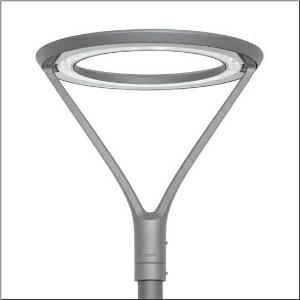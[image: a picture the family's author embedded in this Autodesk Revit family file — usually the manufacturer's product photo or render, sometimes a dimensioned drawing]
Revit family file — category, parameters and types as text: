
# Revit family: dl_r__20___pl1_2s_5xa51283ns008_3424
name_source: partatom
category: Lighting Fixtures
units: mm (PartAtom-declared; Revit-internal decimal feet)

## family parameters
Cut with Voids When Loaded = No
Host = Face
Light Source = No
Part Type = Normal
Room Calculation Point = No
Round Connector Dimension = Use Diameter
Shared = No

## types (1)
- --- (1 x LED, 3060 lm, 23.2 W, 4000K)
    Apparent Load = 23 VA
    CIE Flux Codes = 33 78 99 100 100
    Color Rendering = 70
    Color Temperature = 4000K
    Default Elevation = 1800 mm
    Description = DL® 20, mast luminaire, primary light control with reflector, highly specular, primary optical cover: cover, of toughened safety glass of clear glass with excellent transmission level, light distribution: PL1.2s, light emission: direct distribution, primary light characteristic: symmetric, installation type: post-top, LED, High Power LED, rated luminous flux: 3.030lm, luminous efficacy: 111lm/W, light colour: 740, colour temperature: 4000K, control gear: Plus, control: overheat protection, power reduction, digital communication interface, constant luminous flux control, time-dependent luminous flux control, flexible luminous flux parameterisation, electronic power reduction, mains connection: 230..240V, 50/60Hz, connection cable pre-assembled, cable length: 5m, start of lifetime: 27W, end of service life: 28W, reduction: 14W, luminaire housing, upper part, of cast aluminium, powder-coated, Siteco® metallic grey (DB 702S), diameter: 690mm, height: 690mm, spigot size: 76mm (post-top), mounting height: 4..6m, luminaire housing, of cast aluminium, powder-coated, Siteco® metallic grey (DB 702S), equipment: standard, protection rating (complete): IP66, insulation class (complete): insulation class II (safety insulation), certification: CE, ENEC, VDE, impact resistance: IK08, permissible operating ambient temperature: -25..+35°C, standard-compliant lighting for roads and squares, packaging unit: 1 piece

Light Distribution: PL1.2s
    Height = 690 mm
    Lamp = 1 x LED
    Lamp Light Flux = 3060 lm
    Lamp Power = 23.2 W
    Lamp count = 1
    Length = 690 mm
    Luminous efficacy = 132 lm/W
    Manufacturer = Siteco
    ModVariant = No
    Model = 5XA51283NS008
    Number of Poles = 1
    OnlyDefault = Yes
    Power Factor = 1
    Product Name = DL® 20 | PL1.2s
    Product group = mast luminaire | pylon top
    ProductGroupID = 6100
    Protection Class = Protection class II
    Protection Degree = IP 66
    RLX_Detail_Level = 1
    RLX_Emergency_Light_Flux = 0 lm
    RLX_Emergency_Type = 0
    RLX_Emergency_Type_DB = No
    RlxData = <blob elided: 204313 chars, md5=7895c937>
    Socket = socket
    Standby Power = 0 W
    System Light Flux = 3060 lm
    System Power = 23 W
    Type Comments = factory setting: luminous flux: 100 % | dim-lin: 254 | 310 mA
    Type Image = l_1006001.jpg
    URL = http://relux.com
    VarID = @adj_098159
    Voltage = 0 V
    Weight = 0.00 kg
    Width = 0 mm  [stored 0 ft]

note: [stored X ft] marks values corroborated as IEEE doubles in the binary element streams (Revit-internal decimal feet)

## geometry (parser evidence)
native form markers: Blend x4, Sweep x10
no freeform markers — native parametric forms only
